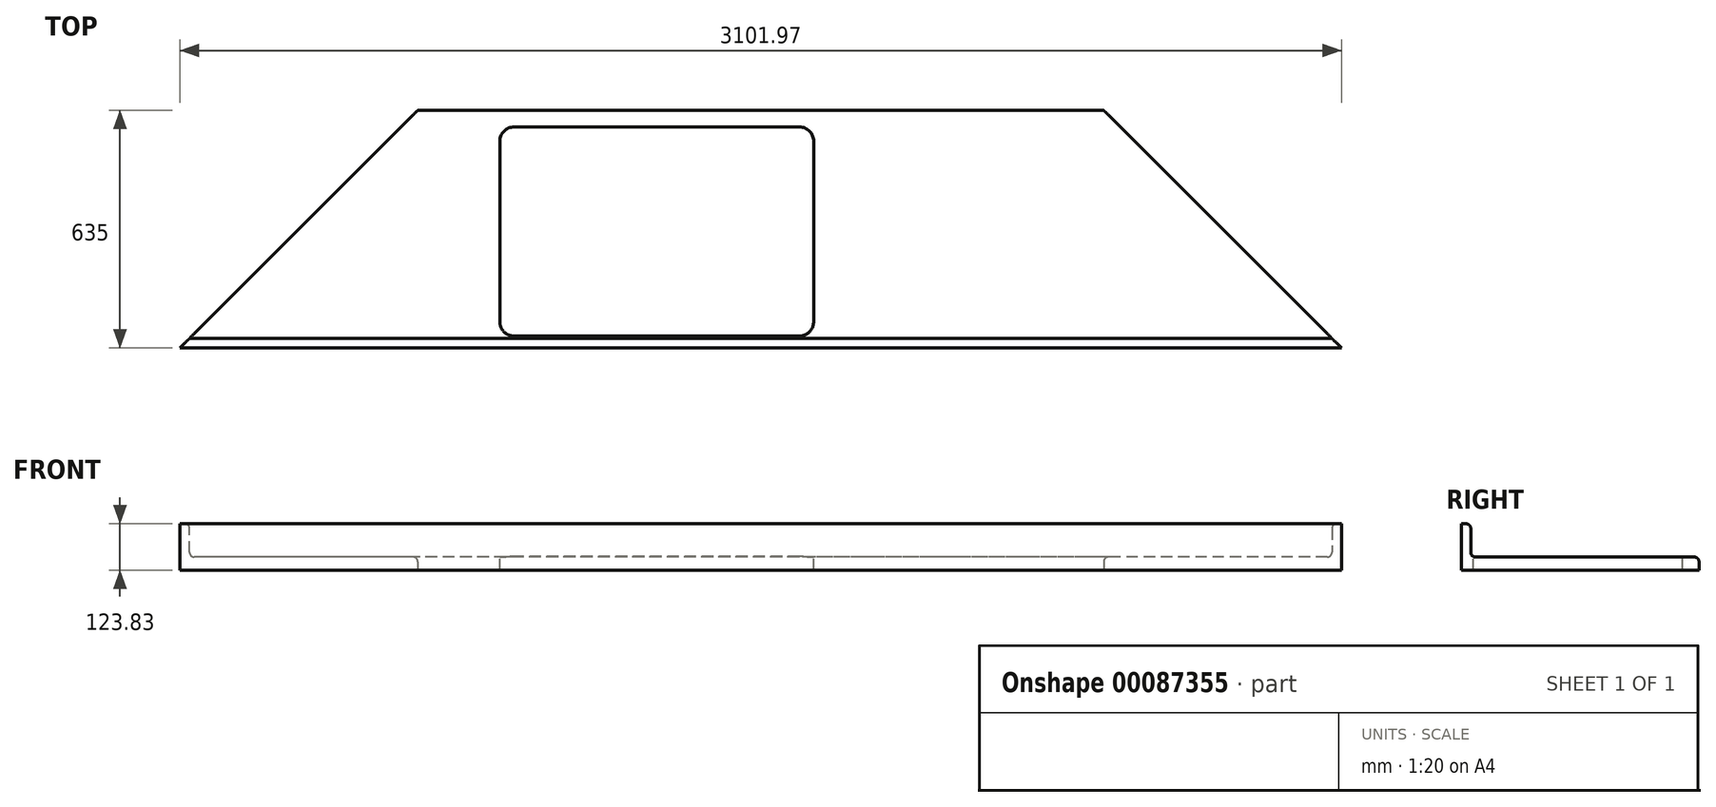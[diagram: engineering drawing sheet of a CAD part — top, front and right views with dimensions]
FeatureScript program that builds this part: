
annotation { "Feature Type Name" : "Feature", "Feature Type Description" : "" }
export const myFeature = defineFeature(function(context is Context, id is Id, definition is map)
    precondition{}
    {
        {
            var Q0;
            Q0=qCreatedBy(makeId("Right.planeOp"),FACE);
            var sketch = newSketch(context, id + "F0", { "sketchPlane" : qUnion([Q0])});
            skLineSegment(sketch, "E0.bottom", {"start": v(0, 0) * mm, "end": v(635, 0) * mm});
            skLineSegment(sketch, "E0.left", {"start": v(0, 0) * mm, "end": v(0, 34.93) * mm});
            skLineSegment(sketch, "E0.right", {"start": v(635, 0) * mm, "end": v(635, 22.23) * mm});
            skLineSegment(sketch, "E1.top", {"start": v(0, 123.83) * mm, "end": v(12.7, 123.83) * mm});
            skLineSegment(sketch, "E1.left", {"start": v(0, 34.93) * mm, "end": v(0, 123.83) * mm});
            skLineSegment(sketch, "E1.right", {"start": v(25.4, 47.63) * mm, "end": v(25.4, 111.12) * mm});
            skPoint(sketch, "E2.visualSharp", {"position": v(25.4, 123.83) * mm});
            skArc(sketch, "E2.filletArc", {"start": v(25.4, 111.12) * mm, "mid": v(21.68, 120.1) * mm, "end": v(12.7, 123.83) * mm});
            skLineSegment(sketch, "E3", {"start": v(622.3, 34.93) * mm, "end": v(38.1, 34.93) * mm});
            skPoint(sketch, "E4.visualSharp", {"position": v(25.4, 34.93) * mm});
            skArc(sketch, "E4.filletArc", {"start": v(25.4, 47.63) * mm, "mid": v(29.12, 38.64) * mm, "end": v(38.1, 34.93) * mm});
            skPoint(sketch, "E5.visualSharp", {"position": v(635, 34.93) * mm});
            skArc(sketch, "E5.filletArc", {"start": v(635, 22.23) * mm, "mid": v(631.28, 31.2) * mm, "end": v(622.3, 34.93) * mm});
            skSolve(sketch);
        }
        {
            var Q0;
            Q0=makeQuery(id+"F0.imprint","IMPRINT",FACE,{"disambiguationData":[TD([[makeQuery(id+"F0.imprint","IMPRINT",EDGE,{"derivedFrom":sQuery(id+"F0.wireOp",EDGE,"E0.bottom")}),1.0]])]});
            extrude(context, id + "F1", {"entities" : qUnion([Q0]), "depth" : 3302 * mm});
        }
        {
            var Q0;
            Q0=makeQuery(id+"F1.opExtrude","SWEPT_FACE",FACE,{"disambiguationData":[OSD([sQuery(id+"F0.wireOp",EDGE,"E0.bottom")])]});
            var sketch = newSketch(context, id + "F2", { "sketchPlane" : qUnion([Q0])});
            skLineSegment(sketch, "E6", {"start": v(3302, 0) * mm, "end": v(2667, -635) * mm});
            skLineSegment(sketch, "E7", {"start": v(835.03, -635) * mm, "end": v(200.02, 0) * mm});
            skLineSegment(sketch, "E8", {"start": v(2667, -635) * mm, "end": v(3302, -635) * mm});
            skLineSegment(sketch, "E9", {"start": v(3302, -635) * mm, "end": v(3302, 0) * mm});
            skLineSegment(sketch, "E10", {"start": v(835.03, -635) * mm, "end": v(0, -635) * mm});
            skLineSegment(sketch, "E11", {"start": v(0, -635) * mm, "end": v(0, 0) * mm});
            skLineSegment(sketch, "E12", {"start": v(0, 0) * mm, "end": v(200.02, 0) * mm});
            skSolve(sketch);
        }
        {
            var Q0;
            Q0 = qSketchRegion(id + "F2", true);
            extrude(context, id + "F3", {"entities" : qUnion([Q0]), "operationType" : NewBodyOperationType.REMOVE, "oppositeDirection" : true, "depth" : 254 * mm});
        }
        {
            var Q0;
            Q0=makeQuery(id+"F1.opExtrude","SWEPT_FACE",FACE,{"disambiguationData":[OSD([sQuery(id+"F0.wireOp",EDGE,"E3")])]});
            var sketch = newSketch(context, id + "F4", { "sketchPlane" : qUnion([Q0])});
            skLineSegment(sketch, "E13.bottom", {"start": v(1854.2, 31.75) * mm, "end": v(1092.2, 31.75) * mm});
            skLineSegment(sketch, "E13.top", {"start": v(1854.2, 590.55) * mm, "end": v(1092.2, 590.55) * mm});
            skLineSegment(sketch, "E13.left", {"start": v(1892.3, 69.85) * mm, "end": v(1892.3, 552.45) * mm});
            skLineSegment(sketch, "E13.right", {"start": v(1054.1, 69.85) * mm, "end": v(1054.1, 552.45) * mm});
            skLineSegment(sketch, "E14", {"start": v(1473.2, -394.82) * mm, "end": v(1473.2, 1065.01) * mm, "construction": true});
            skPoint(sketch, "E15.visualSharp", {"position": v(1892.3, 31.75) * mm});
            skArc(sketch, "E15.filletArc", {"start": v(1854.2, 31.75) * mm, "mid": v(1881.14, 42.9) * mm, "end": v(1892.3, 69.85) * mm});
            skPoint(sketch, "E16.visualSharp", {"position": v(1054.1, 31.75) * mm});
            skArc(sketch, "E16.filletArc", {"start": v(1054.1, 69.85) * mm, "mid": v(1065.26, 42.9) * mm, "end": v(1092.2, 31.75) * mm});
            skPoint(sketch, "E17.visualSharp", {"position": v(1054.1, 590.55) * mm});
            skArc(sketch, "E17.filletArc", {"start": v(1092.2, 590.55) * mm, "mid": v(1065.26, 579.4) * mm, "end": v(1054.1, 552.45) * mm});
            skPoint(sketch, "E18.visualSharp", {"position": v(1892.3, 590.55) * mm});
            skArc(sketch, "E18.filletArc", {"start": v(1892.3, 552.45) * mm, "mid": v(1881.14, 579.4) * mm, "end": v(1854.2, 590.55) * mm});
            skSolve(sketch);
        }
        {
            var Q0;
            Q0 = qSketchRegion(id + "F4", true);
            extrude(context, id + "F5", {"entities" : qUnion([Q0]), "operationType" : NewBodyOperationType.REMOVE, "oppositeDirection" : true, "depth" : 127 * mm});
        }
        {
            var Q0;
            Q0 = qSketchRegion(id + "F4", true);
            extrude(context, id + "F6", {"entities" : qUnion([Q0]), "operationType" : NewBodyOperationType.REMOVE, "depth" : 254 * mm});
        }
    });
